# Revit family: PRD_AR_ShwrFttngsPckg_F3SSelfClosingShower_F3SV20111
name_source: partatom
category: Plumbing Fixtures
units: mm (PartAtom-declared; Revit-internal decimal feet)

## family parameters
Cut with Voids When Loaded = Yes
Enable Cutting in Views = Yes
Host = Face
Maintain Annotation Orientation = No
OmniClass Number = 23.45.05.14.99
OmniClass Title = Other Sanitary Washing Plumbing Fixtures
Part Type = Normal
Room Calculation Point = No
Round Connector Dimension = Use Diameter
Shared = No

## types (1)
- F3SV2011
    AccentColour = chrome-look (glossy)
    AdditionalConnections = No
    AdjustableFlowTime = Yes
    AssetType = Fixed
    BIMObjectName = PRD_AR_ ShowerFittingsPackage_F3SSelfClosingShower_F3SV2011
    BasicColour = stainless steel-look
    BodyMaterial = PRD_AR_StainlessSteel_Brushed
    BuiltinFittingModel = Finishing section
    ButtonMaterial = PRD_AR_ChromatedBrass_HighPolished
    CW Connection = Yes
    CWFU = 0
    Category = Pr_40_20_87_75, Shower fittings package
    Circulation = No
    Color = stainless steel-look
    CompatibleA3000Open = No
    ConnectionWithPayWaterDispenser = not possible
    CoverPlateHeight = 245 mm
    CoverPlateWidth = 190 mm
    Default Elevation = 1219 mm
    Description = F3S self-closing straight-way valve DN 15 as finished installation kit for in-wall installation in basic installation kit, for shower facilities. Especially suitable for facilities at risk of vandalism. Self-closing functional part, hydraulically controlled, piston-free design, self-closing, continuously adjustable flow duration. For connection to pre-mixed hot water or cold water. Housing including shuttle valve seat, pressure cap with safety screws, visible parts, polished chromium-plated brass. Stainless steel cover plate 190 x 245 x 2 mm, mounting from the front with safety screws and rosette. Depth adjustability 20 mm.
    DiameterNominal = DN 15
    DrainSize = 15 mm  [stored 0.0492126 ft]
    Export Type to IFC As = IfcValveType
    Features = For connection to pre-mixed hot water or cold water. Housing including shuttle valve seat, pressure cap with safety screws, visible parts, polished chromium-plated brass. Stainless steel cover plate 190 x 245 x 2 mm.
    Finish = satin finished
    Flow = 0.4 L/s
    ForHandShower = No
    FunctionalPrinciple = Hydraulic self-closing
    HWFU = 0
    HasTray = No
    HygieneFlushing = No
    IfcExportAs = IfcSanitaryTerminalType
    IfcExportType = SHOWER
    InletSize = G 3/4 B
    LockingMechanism = Top section, non-ceramic
    Manufacturer = KWC Group Management AG
    ManufacturerName = KWC Group Management AG
    ManufacturerURL = www.kwc-professional.com
    Material = stainless steel
    MaterialCasing = stainless steel
    MaterialFitting = brass-look
    MaximumFlowTime = 35 Seconds
    MinimumFlowPressure = 1 bar
    MinimumFlowTime = 5 Seconds
    Model = F3SV2011
    ModelNumber = 2030068215
    ModelReference = F3SV2011
    NBSDescription = Shower fittings package
    NBSReference = 45-35-70/330
    Name = F3S Self-closing shower F3SV2011
    NominalDepth = 2 mm  [stored 0.00656168 ft]
    NominalHeight = 245 mm  [stored 0.803806 ft]
    NominalLength = 245 mm  [stored 0.803806 ft]
    NominalWidth = 190 mm
    ProductInformation = http://pim.kwc.com
    ProtectiveShutdown = No
    ShowerPipeDraining = No
    ShowerType = Individual
    Size = 15
    SoundInsulation = No
    Status = NEW
    SurfaceFinishCasing = satin finished
    SurfaceFinishFitting = chromed
    SurfaceTreatmentFitting = polished
    TemperatureLimit = No
    ThermalDisinfection = No
    Type IFC Predefined Type = FLUSHING
    TypeOfMixing = No
    TypeOfMounting = In-wall installation with box
    TypeOfOperation = Manual operation
    TypeOfShower = in-wall fitting
    URL = www.kwc-professional.com
    Uniclass2015Code = Pr_40_20_87_75
    Uniclass2015Title = Shower fittings package
    Uniclass2015Version = Products v1.36
    Vent Connection = Yes
    Version = 1
    VolumeFlowRateAt3Bar = 0.4 l/s
    WFU = 0
    Waste Connection = Yes
    WaterConnection = threaded connection (external)
    WithBackflowPreventer = No
    WithFilter = Yes
    WithRosettesCoverPlate = Yes

note: [stored X ft] marks values corroborated as IEEE doubles in the binary element streams (Revit-internal decimal feet)

## geometry (parser evidence)
native form markers: Sweep x6
no freeform markers — native parametric forms only
